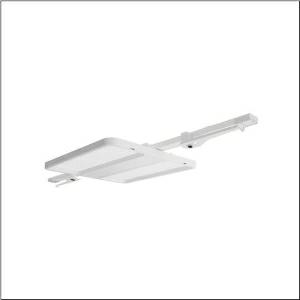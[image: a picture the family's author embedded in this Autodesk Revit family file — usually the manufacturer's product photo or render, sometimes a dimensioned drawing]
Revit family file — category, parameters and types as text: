
# Revit family: highbay_11_fur_modario_r__tragschiene_midi_51hn12da4nma_8ee4
name_source: partatom
category: Lighting Fixtures
units: mm (PartAtom-declared; Revit-internal decimal feet)

## family parameters
Cut with Voids When Loaded = No
Host = Face
Light Source = No
Part Type = Normal
Room Calculation Point = No
Round Connector Dimension = Use Diameter
Shared = No

## types (1)
- --- (1 x LED, 31500 lm, 167.9 W, 4000K)
    Apparent Load = 168 VA
    CIE Flux Codes = 87 98 100 100 100
    Color Rendering = 80
    Color Temperature = 4000K
    Default Elevation = 1800 mm
    Description = high bay luminaire Highbay 11 for Modario® trunking rail midi; direct symmetric wide distribution, light control with lens of PMMA; UGR ≤ 22 (X = 4H | Y = 8H | S = 0.25H | reflection values 70/50/20); luminous flux: 31.500lm; light colour: 840, colour temperature: 4000K, MacAdam ≤ 2 SDCM (initial), colour rendering: CRI > 80; luminous efficacy: 187,6lm/W; rated service life: 100.000h (L95/B50) at AT= 25°C; control: DALI 2; luminaire connection: plug, 5-pole, with phase selectionmains connection: 230..240V, AC 50/60Hz; connected load: 167,9W; protection rating (complete): IP64; insulation class (complete): insulation class I (protective earthing); protection symbol: D; impact resistance: IK07; certification: CE, ENEC, VDE, UKCA; internal wiring halogen-free; luminaire LABS conformity tested according to VDMA 24364:2018-05; corresponds to IFS (International Featured Standards) requirements for safety and quality in the food industry; housing frame of high-performance plastic PA6, matt traffic white (RAL 9016); cover of PMMA; fixing on rail side of steel, galvanised, white; blank cover of PC, traffic white (RAL 9016); dimension (LxWxH): 1.195 x 442 x 72mm; permissible operating ambient temperature: -40..+45°C (reducing of maximum allowable ambient temperature of 5°C with ceiling mounting); packaging unit: 1 piece
    Height = 72 mm  [stored 0.23622 ft]
    Lamp = 1 x LED
    Lamp Light Flux = 31500 lm
    Lamp Power = 167.9 W
    Lamp count = 1
    Length = 474 mm
    Luminous efficacy = 188 lm/W
    Manufacturer = Siteco
    ModVariant = No
    Model = 51HN12DA4NMA
    Mounting Place = Ceiling
    Mounting Type = Pendant
    Number of Poles = 1
    OnlyDefault = Yes
    Power Factor = 1
    Product Name = Highbay 11 für Modario® Tragschiene midi
    Product group = high bay luminaire
    ProductGroupID = 901
    Protection Class = Protection class I
    Protection Degree = IP 64
    RLX_Detail_Level = 1
    RLX_Emergency_Light_Flux = 0 lm
    RLX_Emergency_Type = 0
    RLX_Emergency_Type_DB = No
    RlxData = <blob elided: 18125 chars, md5=b918ecbc>
    Socket = socket
    Standby Power = 0 W
    System Light Flux = 31500 lm
    System Power = 168 W
    Type Comments = factory setting: luminous flux: 100 % | dim-lin: 254 | 754 mA
    Type Image = l_1363266.jpg
    URL = http://relux.com
    VarID = @adj_017659
    Voltage = 0 V
    Weight = 0.00 kg
    Width = 442 mm

note: [stored X ft] marks values corroborated as IEEE doubles in the binary element streams (Revit-internal decimal feet)

## geometry (parser evidence)
native form markers: Blend x4, Sweep x10
no freeform markers — native parametric forms only
